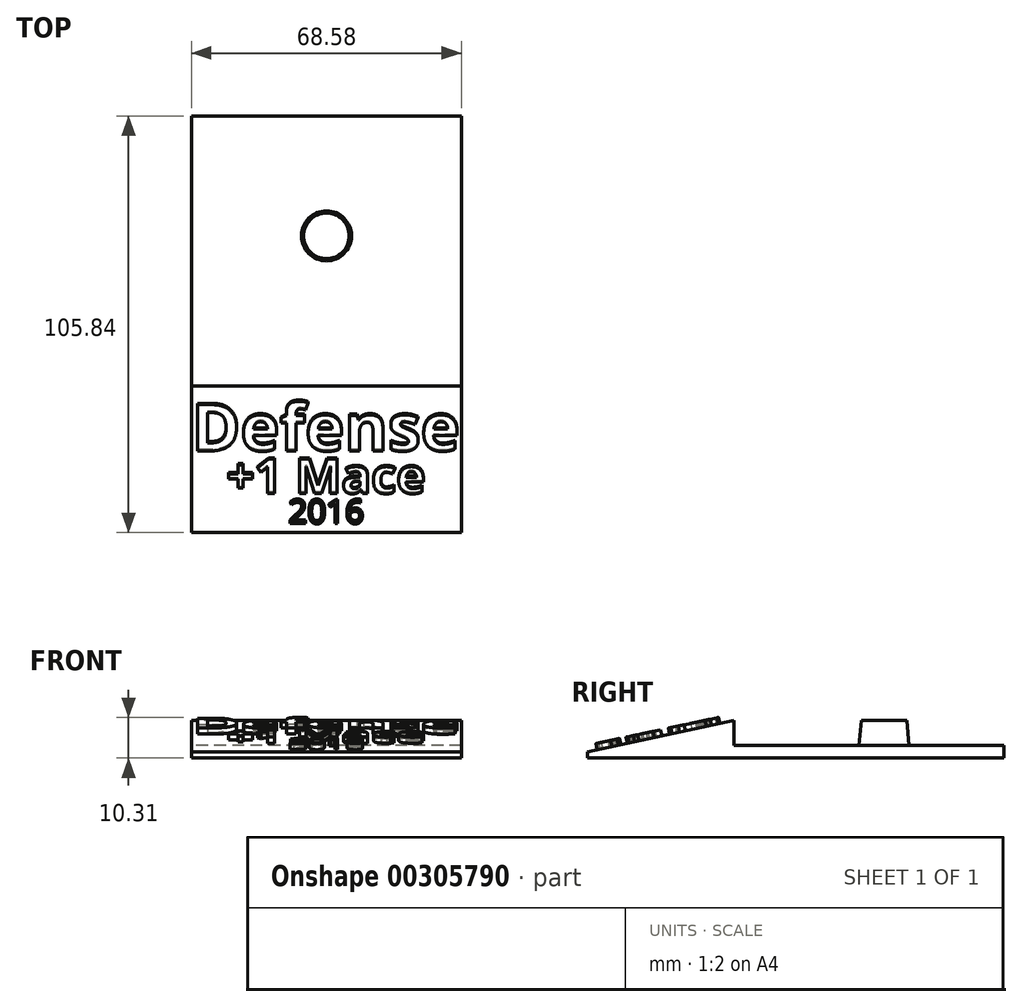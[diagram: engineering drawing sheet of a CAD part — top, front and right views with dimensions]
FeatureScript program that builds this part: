
annotation { "Feature Type Name" : "Feature", "Feature Type Description" : "" }
export const myFeature = defineFeature(function(context is Context, id is Id, definition is map)
    precondition{}
    {
        {
            var Q0;
            Q0=qCreatedBy(makeId("Right.planeOp"),FACE);
            var sketch = newSketch(context, id + "F0", { "sketchPlane" : qUnion([Q0])});
            skLineSegment(sketch, "E0", {"start": v(0, 0) * mm, "end": v(-105.84, 0) * mm});
            skLineSegment(sketch, "E1", {"start": v(-105.84, 0) * mm, "end": v(-105.84, 1.59) * mm});
            skLineSegment(sketch, "E2", {"start": v(-105.84, 1.59) * mm, "end": v(-68.58, 9.52) * mm});
            skLineSegment(sketch, "E3", {"start": v(-68.58, 9.52) * mm, "end": v(-68.58, 3.17) * mm});
            skLineSegment(sketch, "E4", {"start": v(-68.58, 3.17) * mm, "end": v(0, 3.18) * mm});
            skLineSegment(sketch, "E5", {"start": v(0, 3.18) * mm, "end": v(0, 0) * mm});
            skSolve(sketch);
        }
        {
            var Q0;
            Q0=makeQuery(id+"F0.imprint","IMPRINT",FACE,{"disambiguationData":[TD([[makeQuery(id+"F0.imprint","IMPRINT",EDGE,{"derivedFrom":sQuery(id+"F0.wireOp",EDGE,"E0")}),-1.0]])]});
            extrude(context, id + "F1", {"entities" : qUnion([Q0]), "depth" : 68.58 * mm, "symmetric" : true});
        }
        {
            var Q0;
            Q0=makeQuery(id+"F1.opExtrude","SWEPT_FACE",FACE,{"disambiguationData":[OSD([sQuery(id+"F0.wireOp",EDGE,"E4")])]});
            var sketch = newSketch(context, id + "F2", { "sketchPlane" : qUnion([Q0])});
            skLineSegment(sketch, "E6", {"start": v(0, 0) * mm, "end": v(0, -68.58) * mm, "construction": true});
            skCircle(sketch, "E7", {"center": v(0, -30.48) * mm, "radius": 6.35 * mm});
            skSolve(sketch);
        }
        {
            var Q0;
            Q0=makeQuery(id+"F2.imprint","IMPRINT",FACE,{"disambiguationData":[TD([[makeQuery(id+"F2.imprint","IMPRINT",EDGE,{"derivedFrom":sQuery(id+"F2.wireOp",EDGE,"E7")}),1.0]])]});
            extrude(context, id + "F3", {"entities" : qUnion([Q0]), "operationType" : NewBodyOperationType.ADD, "depth" : 6.35 * mm, "hasDraft" : true, "draftAngle" : 5 * degree, "draftPullDirection" : true});
        }
        {
            var Q0;
            Q0=makeQuery(id+"F1.opExtrude","SWEPT_FACE",FACE,{"disambiguationData":[OSD([sQuery(id+"F0.wireOp",EDGE,"E2")])]});
            var sketch = newSketch(context, id + "F4", { "sketchPlane" : qUnion([Q0])});
            skText(sketch, "E8", { "text": "Defense \n\n", "fontName": "OpenSans-Bold.ttf"});
            skText(sketch, "E9", { "text": "+1 Mace \n", "fontName": "OpenSans-Bold.ttf"});
            skText(sketch, "E10", { "text": "2016", "fontName": "OpenSans-Regular.ttf"});
            skLineSegment(sketch, "E11", {"start": v(0, -65.1) * mm, "end": v(0, -103.2) * mm, "construction": true});
            const initialGuessF4  = {"E8": [-0.0343, -0.08166, 1, 0, 0.01211], "E9": [-0.0254, -0.09271, 1, 0, 0.00898], "E10": [-0.00965, -0.10057, 1, 0, 0.00604]};
            skSetInitialGuess(sketch, initialGuessF4);
            skSolve(sketch);
        }
        {
            var Q0;
            Q0 = qSketchRegion(id + "F4", true);
            extrude(context, id + "F5", {"entities" : qUnion([Q0]), "operationType" : NewBodyOperationType.ADD, "depth" : 1.59 * mm});
        }
    });
